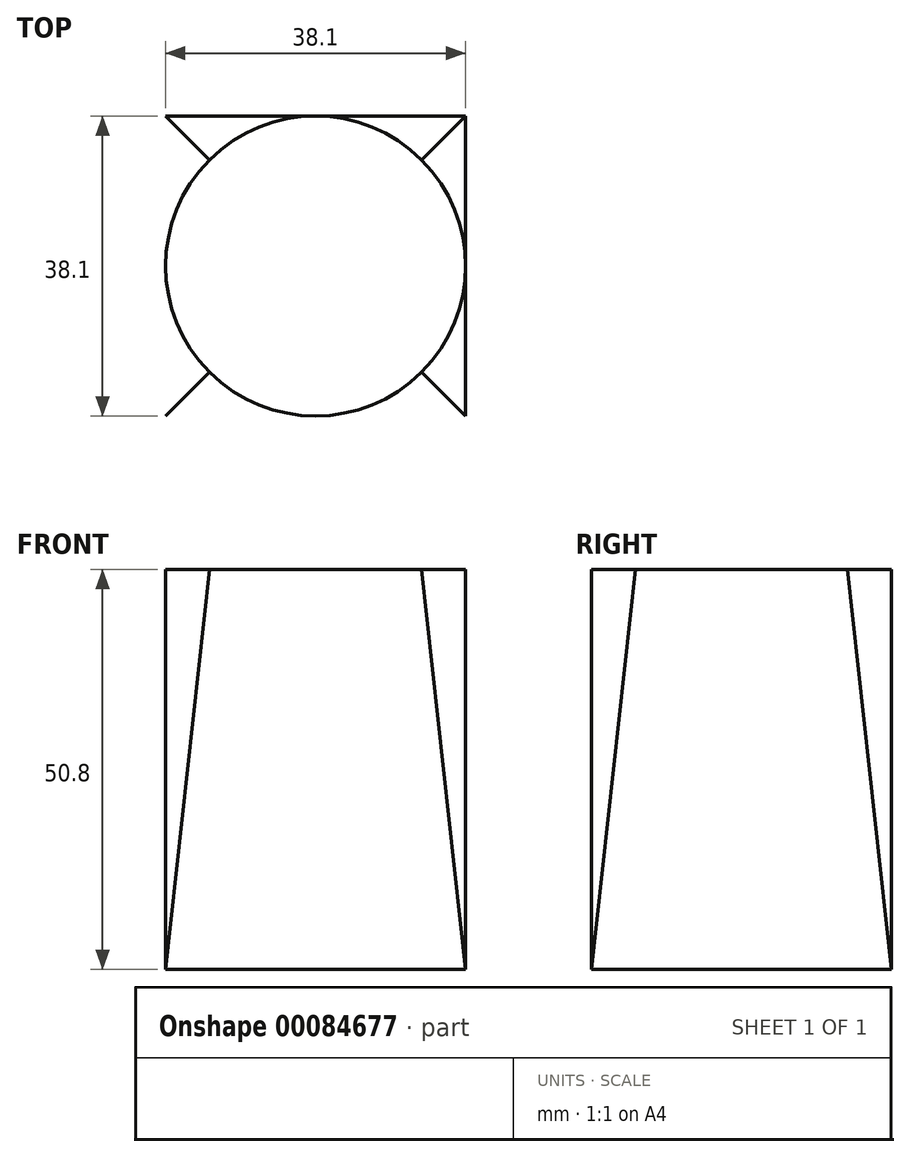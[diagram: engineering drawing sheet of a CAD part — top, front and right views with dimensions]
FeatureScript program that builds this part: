
annotation { "Feature Type Name" : "Feature", "Feature Type Description" : "" }
export const myFeature = defineFeature(function(context is Context, id is Id, definition is map)
    precondition{}
    {
        {
            var Q0;
            Q0=qCreatedBy(makeId("Front.planeOp"),FACE);
            var sketch = newSketch(context, id + "F0", { "sketchPlane" : qUnion([Q0])});
            skLineSegment(sketch, "E0", {"start": v(-19.05, 0) * mm, "end": v(-19.05, 50.8) * mm});
            skSolve(sketch);
        }
        {
            var Q0;
            Q0=qCreatedBy(makeId("Top.planeOp"),FACE);
            var sketch = newSketch(context, id + "F1", { "sketchPlane" : qUnion([Q0])});
            skLineSegment(sketch, "E1.bottom", {"start": v(-19.05, 19.05) * mm, "end": v(19.05, 19.05) * mm});
            skLineSegment(sketch, "E1.top", {"start": v(-19.05, -19.05) * mm, "end": v(19.05, -19.05) * mm});
            skLineSegment(sketch, "E1.left", {"start": v(-19.05, 19.05) * mm, "end": v(-19.05, -19.05) * mm});
            skLineSegment(sketch, "E1.right", {"start": v(19.05, 19.05) * mm, "end": v(19.05, -19.05) * mm});
            skPoint(sketch, "E1.middle", {"position": v(0, 0) * mm});
            skSolve(sketch);
        }
        {
            var Q0;
            Q0=qCreatedBy(makeId("Top.planeOp"),FACE);
            var Q1;
            Q1=sQuery(id+"F0.wireOp",VERTEX,"E0.end");
            cPlane(context, id + "F2", {"entities" : qUnion([Q0, Q1]), "cplaneType" : CPlaneType.PLANE_POINT, "offset" : 152.4 * mm, "width" : 152.4 * mm, "height" : 152.4 * mm});
        }
        {
            var Q0;
            Q0=qCreatedBy(id+"F2.planeOp",FACE);
            var sketch = newSketch(context, id + "F3", { "sketchPlane" : qUnion([Q0])});
            skCircle(sketch, "E2", {"center": v(0, 0) * mm, "radius": 19.05 * mm});
            skSolve(sketch);
        }
        {
            var Q0;
            Q0 = qSketchRegion(id + "F1", true);
            var Q1;
            Q1 = qSketchRegion(id + "F3", true);
            loft(context, id + "F4", {"sheetProfilesArray" : [{ "sheetProfileEntities" : qUnion([Q0]) }, { "sheetProfileEntities" : qUnion([Q1]) }]});
        }
    });
